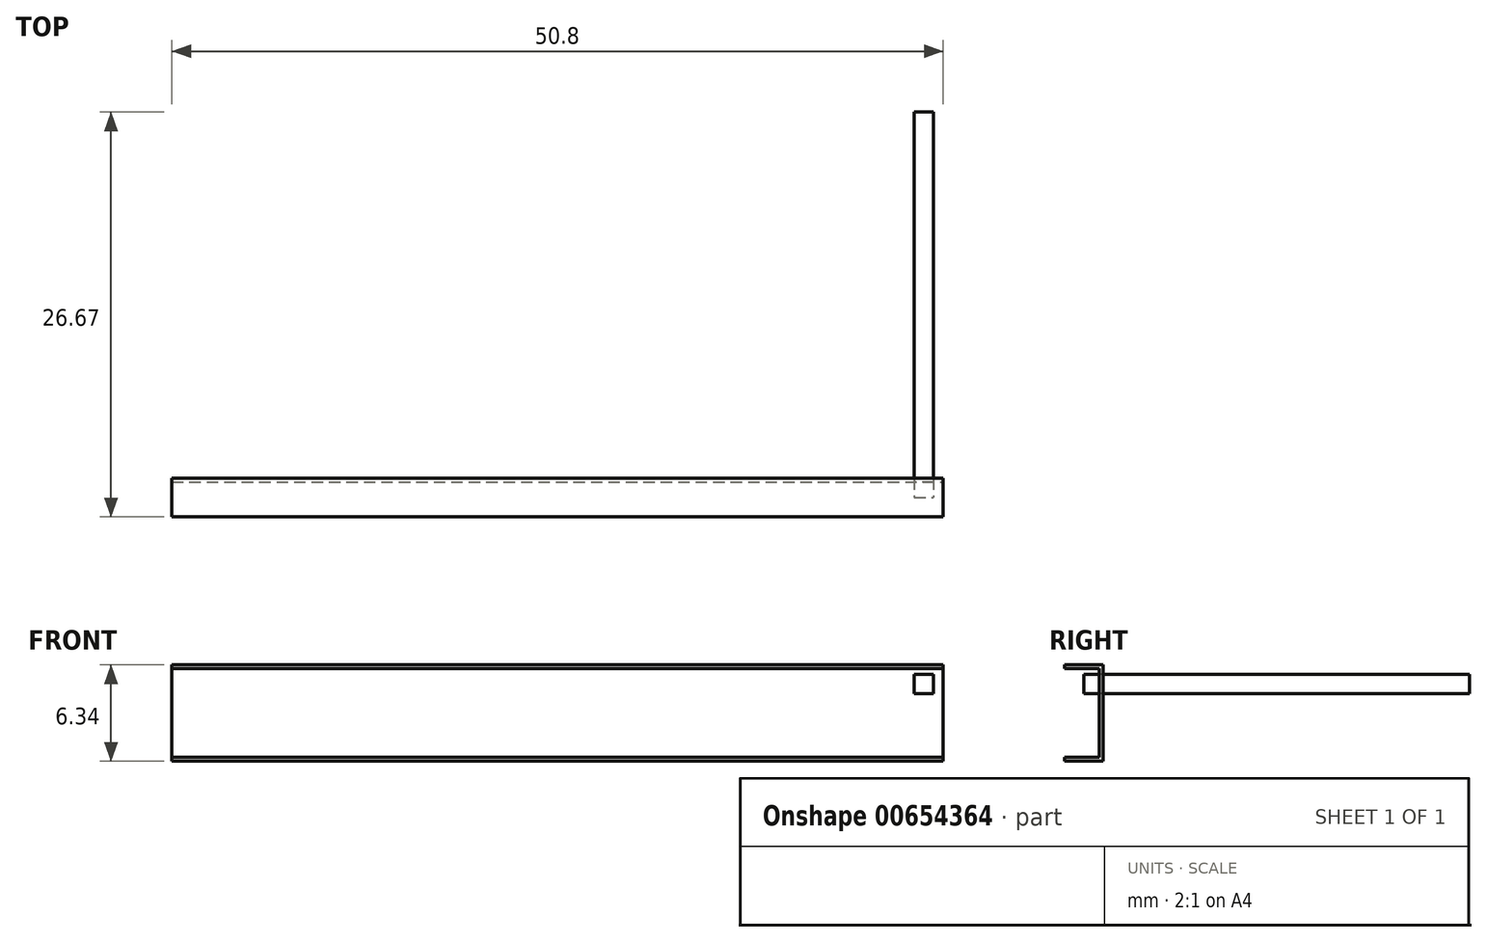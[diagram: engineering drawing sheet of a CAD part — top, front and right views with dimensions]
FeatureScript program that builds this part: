
annotation { "Feature Type Name" : "Feature", "Feature Type Description" : "" }
export const myFeature = defineFeature(function(context is Context, id is Id, definition is map)
    precondition{}
    {
        {
            var Q0;
            Q0=qCreatedBy(makeId("Right.planeOp"),FACE);
            var sketch = newSketch(context, id + "F0", { "sketchPlane" : qUnion([Q0])});
            skLineSegment(sketch, "E0.bottom", {"start": v(-1.27, 3.17) * mm, "end": v(1.27, 3.17) * mm});
            skLineSegment(sketch, "E0.top", {"start": v(-1.27, -3.17) * mm, "end": v(1.27, -3.17) * mm});
            skLineSegment(sketch, "E0.left", {"start": v(-1.27, 3.17) * mm, "end": v(-1.27, -3.17) * mm});
            skLineSegment(sketch, "E0.right", {"start": v(1.27, 3.17) * mm, "end": v(1.27, -3.17) * mm});
            skPoint(sketch, "E0.middle", {"position": v(0, 0) * mm});
            skSolve(sketch);
        }
        {
            var Q0;
            Q0 = qSketchRegion(id + "F0", true);
            extrude(context, id + "F1", {"entities" : qUnion([Q0]), "oppositeDirection" : true, "depth" : 50.8 * mm, "offsetDistance" : 25.4 * mm});
        }
        {
            var Q0;
            Q0=qCreatedBy(makeId("Right.planeOp"),FACE);
            var sketch = newSketch(context, id + "F2", { "sketchPlane" : qUnion([Q0])});
            skLineSegment(sketch, "E1.bottom", {"start": v(1.02, 2.92) * mm, "end": v(-1.52, 2.92) * mm});
            skLineSegment(sketch, "E1.top", {"start": v(1.02, -2.92) * mm, "end": v(-1.52, -2.92) * mm});
            skLineSegment(sketch, "E1.left", {"start": v(1.02, 2.92) * mm, "end": v(1.02, -2.92) * mm});
            skLineSegment(sketch, "E1.right", {"start": v(-1.52, 2.92) * mm, "end": v(-1.52, -2.92) * mm});
            skPoint(sketch, "E1.middle", {"position": v(0, 0) * mm});
            skSolve(sketch);
        }
        {
            var Q0;
            Q0 = qSketchRegion(id + "F2", true);
            extrude(context, id + "F3", {"entities" : qUnion([Q0]), "operationType" : NewBodyOperationType.REMOVE, "oppositeDirection" : true, "depth" : 76.2 * mm, "offsetDistance" : 25.4 * mm});
        }
        {
            var Q0;
            Q0=qCreatedBy(makeId("Front.planeOp"),FACE);
            var sketch = newSketch(context, id + "F4", { "sketchPlane" : qUnion([Q0])});
            skLineSegment(sketch, "E2.bottom", {"start": v(-1.9, 2.54) * mm, "end": v(-0.63, 2.54) * mm});
            skLineSegment(sketch, "E2.top", {"start": v(-1.9, 1.27) * mm, "end": v(-0.63, 1.27) * mm});
            skLineSegment(sketch, "E2.left", {"start": v(-1.9, 2.54) * mm, "end": v(-1.9, 1.27) * mm});
            skLineSegment(sketch, "E2.right", {"start": v(-0.63, 2.54) * mm, "end": v(-0.63, 1.27) * mm});
            skPoint(sketch, "E2.middle", {"position": v(0, 0) * mm});
            skSolve(sketch);
        }
        {
            var Q0;
            Q0 = qSketchRegion(id + "F4", true);
            extrude(context, id + "F5", {"entities" : qUnion([Q0]), "oppositeDirection" : true, "depth" : 25.4 * mm, "offsetDistance" : 25.4 * mm});
        }
    });
